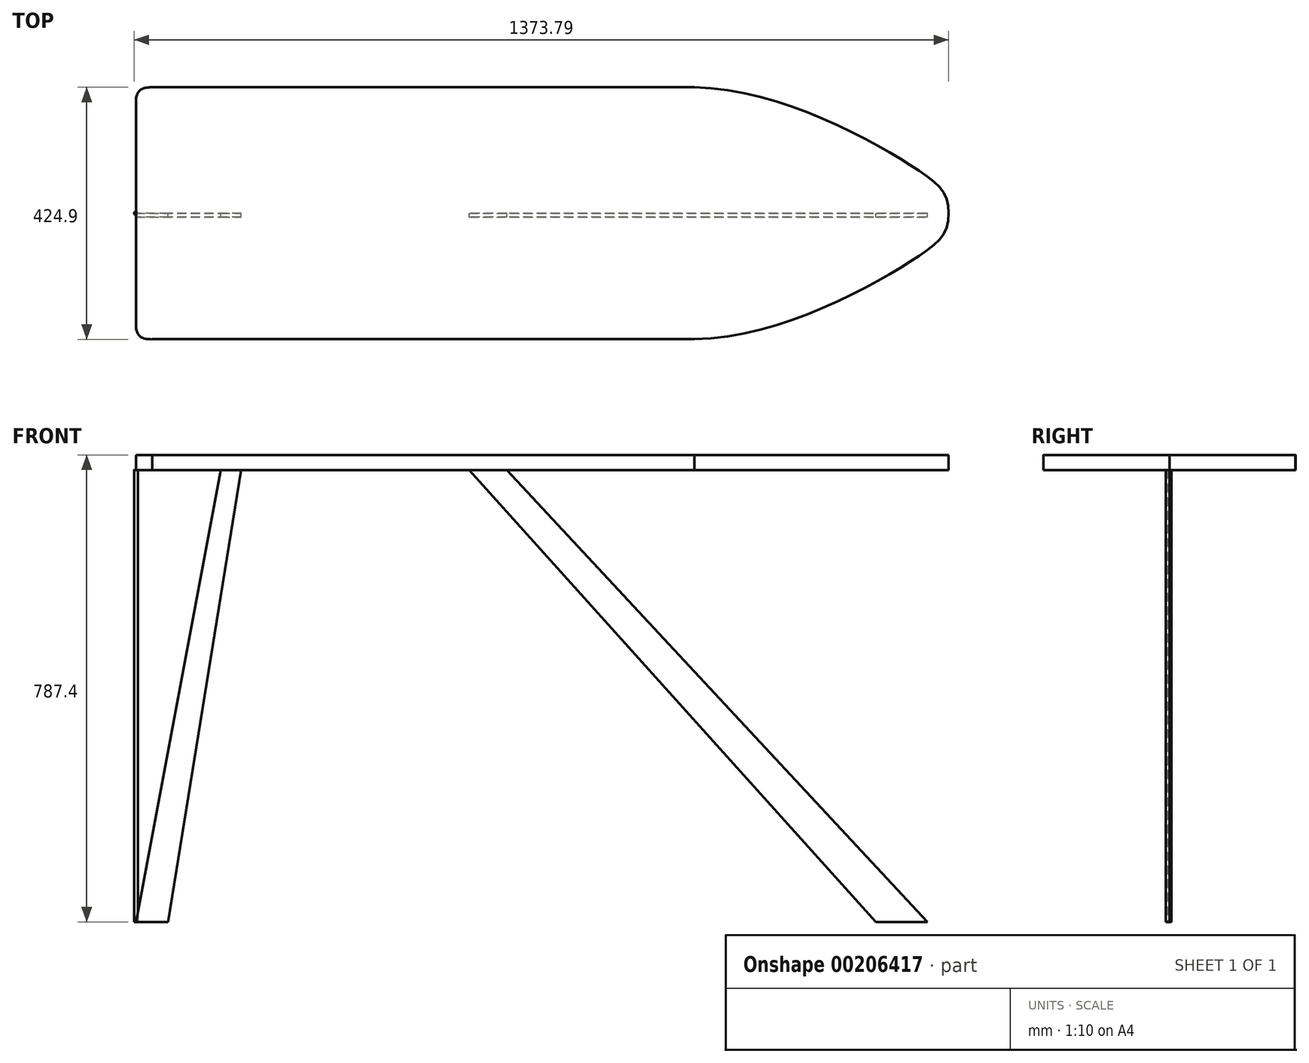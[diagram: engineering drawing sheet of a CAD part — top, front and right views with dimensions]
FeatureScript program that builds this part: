
annotation { "Feature Type Name" : "Feature", "Feature Type Description" : "" }
export const myFeature = defineFeature(function(context is Context, id is Id, definition is map)
    precondition{}
    {
        {
            var Q0;
            Q0=qCreatedBy(makeId("Front.planeOp"),FACE);
            var sketch = newSketch(context, id + "F0", { "sketchPlane" : qUnion([Q0])});
            skLineSegment(sketch, "E0", {"start": v(0, 762) * mm, "end": v(1371.6, 762) * mm, "construction": true});
            skLineSegment(sketch, "E1", {"start": v(0, 0) * mm, "end": v(143.16, 762) * mm});
            skLineSegment(sketch, "E2", {"start": v(143.16, 762) * mm, "end": v(177.02, 762) * mm});
            skLineSegment(sketch, "E3", {"start": v(177.02, 762) * mm, "end": v(54.27, 0) * mm});
            skLineSegment(sketch, "E4", {"start": v(54.27, 0) * mm, "end": v(0, 0) * mm});
            skLineSegment(sketch, "E5", {"start": v(1334.63, 0) * mm, "end": v(625.67, 762) * mm});
            skLineSegment(sketch, "E6", {"start": v(625.67, 762) * mm, "end": v(562.18, 762) * mm});
            skLineSegment(sketch, "E7", {"start": v(562.18, 762) * mm, "end": v(1247.87, 0) * mm});
            skLineSegment(sketch, "E8", {"start": v(1247.87, 0) * mm, "end": v(1334.63, 0) * mm});
            skSolve(sketch);
        }
        {
            var Q0;
            Q0=qCreatedBy(makeId("Top.planeOp"),FACE);
            var sketch = newSketch(context, id + "F1", { "sketchPlane" : qUnion([Q0])});
            skCircle(sketch, "E9", {"center": v(0, 0) * mm, "radius": 3.18 * mm});
            skSolve(sketch);
        }
        {
            var Q0;
            Q0 = qSketchRegion(id + "F1", true);
            extrude(context, id + "F2", {"entities" : qUnion([Q0]), "depth" : 762 * mm});
        }
        {
            var Q0;
            Q0=makeQuery(id+"F0.imprint","IMPRINT",FACE,{"disambiguationData":[TD([[makeQuery(id+"F0.imprint","IMPRINT",EDGE,{"derivedFrom":sQuery(id+"F0.wireOp",EDGE,"E5")}),1.0]])]});
            var Q1;
            Q1=makeQuery(id+"F0.imprint","IMPRINT",FACE,{"disambiguationData":[TD([[makeQuery(id+"F0.imprint","IMPRINT",EDGE,{"derivedFrom":sQuery(id+"F0.wireOp",EDGE,"E1")}),-1.0]])]});
            extrude(context, id + "F3", {"entities" : qUnion([Q0, Q1]), "depth" : 6.35 * mm});
        }
        {
            var Q0;
            Q0=makeQuery(id+"F2.opExtrude","CAP_FACE",FACE,{"disambiguationData":[OSD([sQuery(id+"F1.wireOp",EDGE,"E9")])],"isStart":false});
            var sketch = newSketch(context, id + "F4", { "sketchPlane" : qUnion([Q0])});
            skLineSegment(sketch, "E10", {"start": v(0, 0) * mm, "end": v(0, 190.5) * mm});
            skLineSegment(sketch, "E11", {"start": v(27.09, 212.43) * mm, "end": v(941.49, 212.43) * mm});
            skFitSpline(sketch, "E12", {"points": [v(0, 190.5) * mm, v(27.09, 212.43) * mm], "startDerivative": vector(0, 53.48) * mm, "endDerivative": vector(45.42, -1.19) * mm});
            skFitSpline(sketch, "E13", {"points": [v(941.49, 212.43) * mm, v(1311.04, 78) * mm, v(1370.51, 0) * mm], "startDerivative": vector(641.51, -13.24) * mm, "endDerivative": vector(-15.88, -316.52) * mm});
            skLineSegment(sketch, "E14.MirrorCS", {"start": v(0, 0) * mm, "end": v(0, -190.5) * mm});
            skFitSpline(sketch, "E15.MirrorCS", {"points": [v(941.49, -212.43) * mm, v(1311.04, -78) * mm, v(1370.51, 0) * mm], "startDerivative": vector(641.51, 13.24) * mm, "endDerivative": vector(-15.88, 316.52) * mm});
            skLineSegment(sketch, "E16.MirrorCS", {"start": v(27.09, -212.43) * mm, "end": v(941.49, -212.43) * mm});
            skFitSpline(sketch, "E17.MirrorCS", {"points": [v(0, -190.5) * mm, v(27.09, -212.43) * mm], "startDerivative": vector(0, -53.48) * mm, "endDerivative": vector(45.42, 1.19) * mm});
            skSolve(sketch);
        }
        {
            var Q0;
            Q0 = qSketchRegion(id + "F4", true);
            extrude(context, id + "F5", {"entities" : qUnion([Q0]), "depth" : 25.4 * mm});
        }
    });
